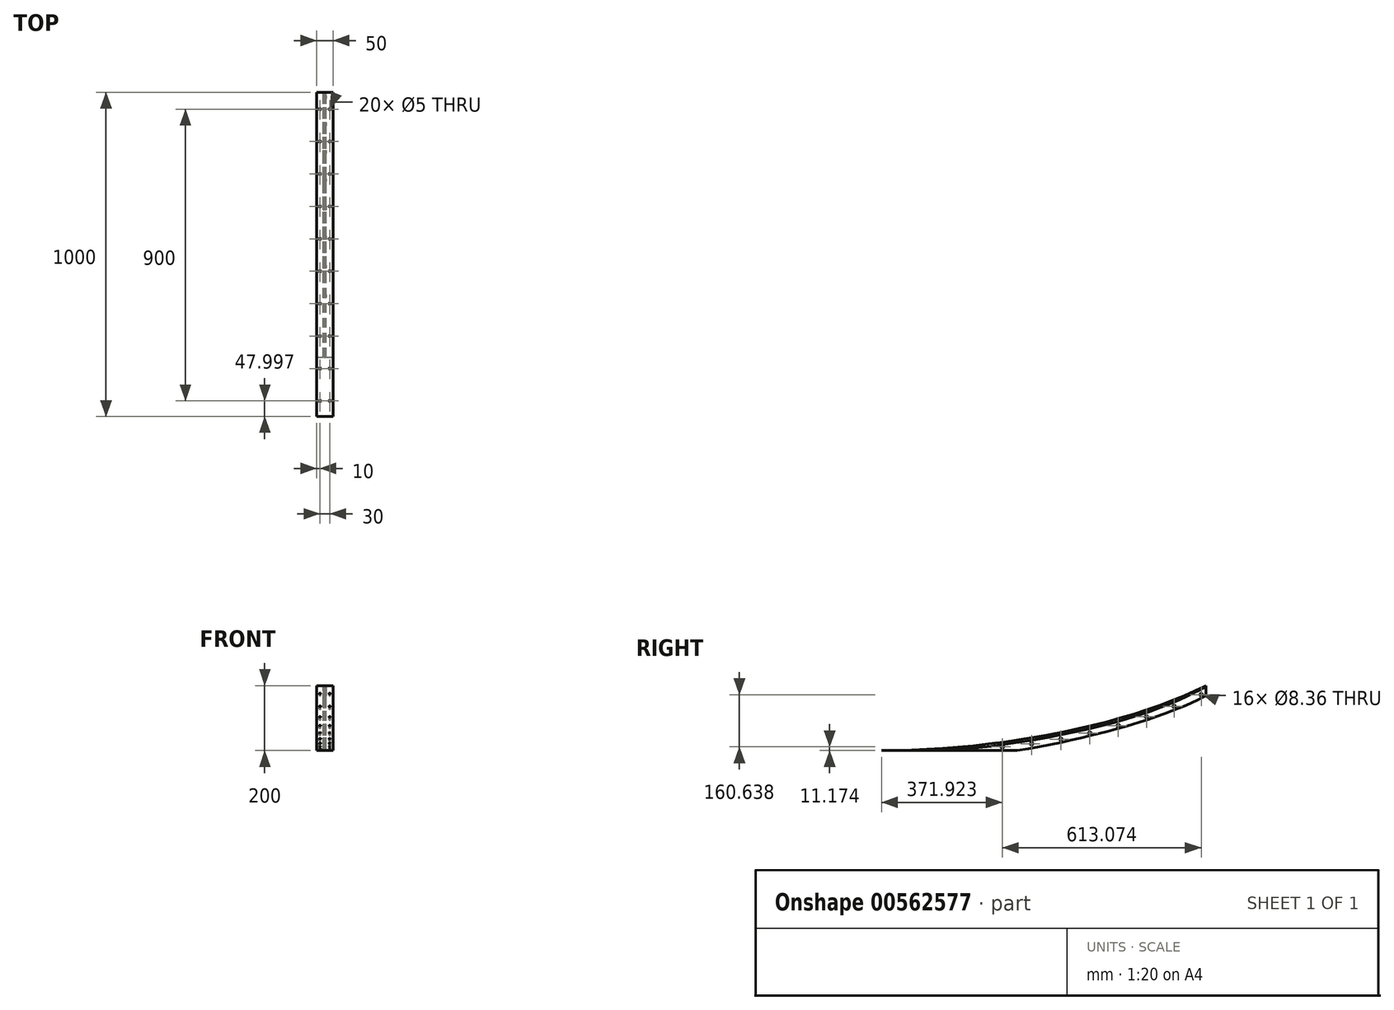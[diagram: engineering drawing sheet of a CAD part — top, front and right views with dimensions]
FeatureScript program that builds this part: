
annotation { "Feature Type Name" : "Feature", "Feature Type Description" : "" }
export const myFeature = defineFeature(function(context is Context, id is Id, definition is map)
    precondition{}
    {
        {
            var Q0;
            Q0=qCreatedBy(makeId("Right.planeOp"),FACE);
            var sketch = newSketch(context, id + "F0", { "sketchPlane" : qUnion([Q0])});
            skFitSpline(sketch, "E0", {"points": [v(-542.95, -39.95) * mm, v(457.05, 160.05) * mm], "startDerivative": vector(1064.65, 0) * mm, "endDerivative": vector(757.35, 377.28) * mm});
            skFitSpline(sketch, "E1.0", {"points": [v(-542.95, -42.95) * mm, v(-454.13, -42.95) * mm, v(-271.77, -33.66) * mm, v(-0.77, 6) * mm, v(251.07, 69.3) * mm, v(395.1, 125.84) * mm, v(458.38, 157.36) * mm]});
            skFitSpline(sketch, "E2.0", {"points": [v(-542.95, -67.95) * mm, v(-453.26, -67.95) * mm, v(-269.31, -58.57) * mm, v(-41.54, -25.24) * mm, v(131.25, 13.4) * mm, v(254.1, 48.12) * mm, v(368.23, 88.4) * mm, v(437.17, 118.87) * mm, v(469.53, 134.99) * mm]});
            skLineSegment(sketch, "E3", {"start": v(457.05, 160.05) * mm, "end": v(457.05, 100.76) * mm});
            skLineSegment(sketch, "E4", {"start": v(-542.95, -39.95) * mm, "end": v(-47.7, -39.95) * mm});
            skSolve(sketch);
        }
        {
            var Q0;
            {var subQ0=sQuery(id+"F0.wireOp",EDGE,"E0");Q0=makeQuery(id+"F0.imprint","IMPRINT",FACE,{"disambiguationData":[TD([[makeQuery(id+"F0.imprint","IMPRINT",EDGE,{"derivedFrom":subQ0}),-1.0]])]});}
            extrude(context, id + "F1", {"entities" : qUnion([Q0]), "endBound" : BoundingType.SYMMETRIC, "depth" : 50 * mm, "offsetDistance" : 25 * mm});
        }
        {
            var Q0;
            {var subQ0=sQuery(id+"F0.wireOp",EDGE,"E3");var subQ1=sQuery(id+"F0.wireOp",EDGE,"E1.0");var subQ2=makeQuery(id+"F0.imprint","INTERSECT",VERTEX,{"derivedFrom":[subQ1,subQ0]});Q0=makeQuery(id+"F0.imprint","IMPRINT",FACE,{"disambiguationData":[TD([[makeQuery(id+"F0.imprint","IMPRINT",EDGE,{"disambiguationData":[TD([[subQ2,1.0]])],"derivedFrom":subQ1}),-1.0]])]});}
            extrude(context, id + "F2", {"entities" : qUnion([Q0]), "operationType" : NewBodyOperationType.ADD, "endBound" : BoundingType.SYMMETRIC, "depth" : 9 * mm, "offsetDistance" : 25 * mm});
        }
        {
            var Q0;
            {var subQ0=sQuery(id+"F0.wireOp",EDGE,"E3");var subQ1=sQuery(id+"F0.wireOp",EDGE,"E1.0");var subQ2=makeQuery(id+"F0.imprint","INTERSECT",VERTEX,{"derivedFrom":[subQ1,subQ0]});Q0=makeQuery(id+"F0.imprint","IMPRINT",FACE,{"disambiguationData":[TD([[makeQuery(id+"F0.imprint","IMPRINT",EDGE,{"disambiguationData":[TD([[subQ2,1.0]])],"derivedFrom":subQ1}),-1.0]])]});}
            extrude(context, id + "F3", {"entities" : qUnion([Q0]), "operationType" : NewBodyOperationType.REMOVE, "endBound" : BoundingType.SYMMETRIC, "oppositeDirection" : true, "depth" : 3 * mm, "offsetDistance" : 25 * mm});
        }
        {
            var Q0;
            Q0=qCreatedBy(makeId("Top.planeOp"),FACE);
            var sketch = newSketch(context, id + "F4", { "sketchPlane" : qUnion([Q0])});
            skCircle(sketch, "E5", {"center": v(15, -494.95) * mm, "radius": 2.5 * mm});
            skCircle(sketch, "E6.0.1.0", {"center": v(15, -394.95) * mm, "radius": 2.5 * mm});
            skCircle(sketch, "E6.0.2.0", {"center": v(15, -294.95) * mm, "radius": 2.5 * mm});
            skCircle(sketch, "E6.0.3.0", {"center": v(15, -194.95) * mm, "radius": 2.5 * mm});
            skCircle(sketch, "E6.0.4.0", {"center": v(15, -94.95) * mm, "radius": 2.5 * mm});
            skCircle(sketch, "E6.0.5.0", {"center": v(15, 5.05) * mm, "radius": 2.5 * mm});
            skCircle(sketch, "E6.0.6.0", {"center": v(15, 105.05) * mm, "radius": 2.5 * mm});
            skCircle(sketch, "E6.0.7.0", {"center": v(15, 205.05) * mm, "radius": 2.5 * mm});
            skCircle(sketch, "E6.0.8.0", {"center": v(15, 305.05) * mm, "radius": 2.5 * mm});
            skCircle(sketch, "E6.0.9.0", {"center": v(15, 405.05) * mm, "radius": 2.5 * mm});
            skCircle(sketch, "E6.1.0.0", {"center": v(-15, -494.95) * mm, "radius": 2.5 * mm});
            skCircle(sketch, "E6.1.1.0", {"center": v(-15, -394.95) * mm, "radius": 2.5 * mm});
            skCircle(sketch, "E6.1.2.0", {"center": v(-15, -294.95) * mm, "radius": 2.5 * mm});
            skCircle(sketch, "E6.1.3.0", {"center": v(-15, -194.95) * mm, "radius": 2.5 * mm});
            skCircle(sketch, "E6.1.4.0", {"center": v(-15, -94.95) * mm, "radius": 2.5 * mm});
            skCircle(sketch, "E6.1.5.0", {"center": v(-15, 5.05) * mm, "radius": 2.5 * mm});
            skCircle(sketch, "E6.1.6.0", {"center": v(-15, 105.05) * mm, "radius": 2.5 * mm});
            skCircle(sketch, "E6.1.7.0", {"center": v(-15, 205.05) * mm, "radius": 2.5 * mm});
            skCircle(sketch, "E6.1.8.0", {"center": v(-15, 305.05) * mm, "radius": 2.5 * mm});
            skCircle(sketch, "E6.1.9.0", {"center": v(-15, 405.05) * mm, "radius": 2.5 * mm});
            skLineSegment(sketch, "E6.direction1", {"start": v(15, -494.95) * mm, "end": v(-15, -494.95) * mm, "construction": true});
            skLineSegment(sketch, "E6.direction2", {"start": v(15, -494.95) * mm, "end": v(15, -394.95) * mm, "construction": true});
            skSolve(sketch);
        }
        {
            var Q0;
            Q0 = qSketchRegion(id + "F4", true);
            extrude(context, id + "F5", {"entities" : qUnion([Q0]), "operationType" : NewBodyOperationType.REMOVE, "endBound" : BoundingType.SYMMETRIC, "oppositeDirection" : true, "depth" : 300 * mm, "offsetDistance" : 25 * mm});
        }
        {
            var Q0;
            Q0=qCreatedBy(makeId("Right.planeOp"),FACE);
            var sketch = newSketch(context, id + "F6", { "sketchPlane" : qUnion([Q0])});
            skCircle(sketch, "E7", {"center": v(442.05, 131.86) * mm, "radius": 4.18 * mm});
            skCircle(sketch, "E8.1.0", {"center": v(358.45, 95.94) * mm, "radius": 4.18 * mm});
            skCircle(sketch, "E8.2.0", {"center": v(273.16, 64.23) * mm, "radius": 4.18 * mm});
            skCircle(sketch, "E8.3.0", {"center": v(186.4, 36.8) * mm, "radius": 4.18 * mm});
            skCircle(sketch, "E8.4.0", {"center": v(98.38, 13.74) * mm, "radius": 4.18 * mm});
            skCircle(sketch, "E8.5.0", {"center": v(9.32, -4.9) * mm, "radius": 4.18 * mm});
            skCircle(sketch, "E8.6.0", {"center": v(-80.55, -19.09) * mm, "radius": 4.18 * mm});
            skCircle(sketch, "E8.7.0", {"center": v(-171.03, -28.78) * mm, "radius": 4.18 * mm});
            skPoint(sketch, "E8.center", {"position": v(-320, 1790) * mm});
            skLineSegment(sketch, "E8.anchor1", {"start": v(-320, 1790) * mm, "end": v(442.05, 131.86) * mm, "construction": true});
            skLineSegment(sketch, "E8.anchor2", {"start": v(-320, 1790) * mm, "end": v(-171.03, -28.78) * mm, "construction": true});
            skSolve(sketch);
        }
        {
            var Q0;
            Q0 = qSketchRegion(id + "F6", true);
            extrude(context, id + "F7", {"entities" : qUnion([Q0]), "operationType" : NewBodyOperationType.REMOVE, "endBound" : BoundingType.SYMMETRIC, "oppositeDirection" : true, "depth" : 25 * mm, "offsetDistance" : 25 * mm});
        }
    });
